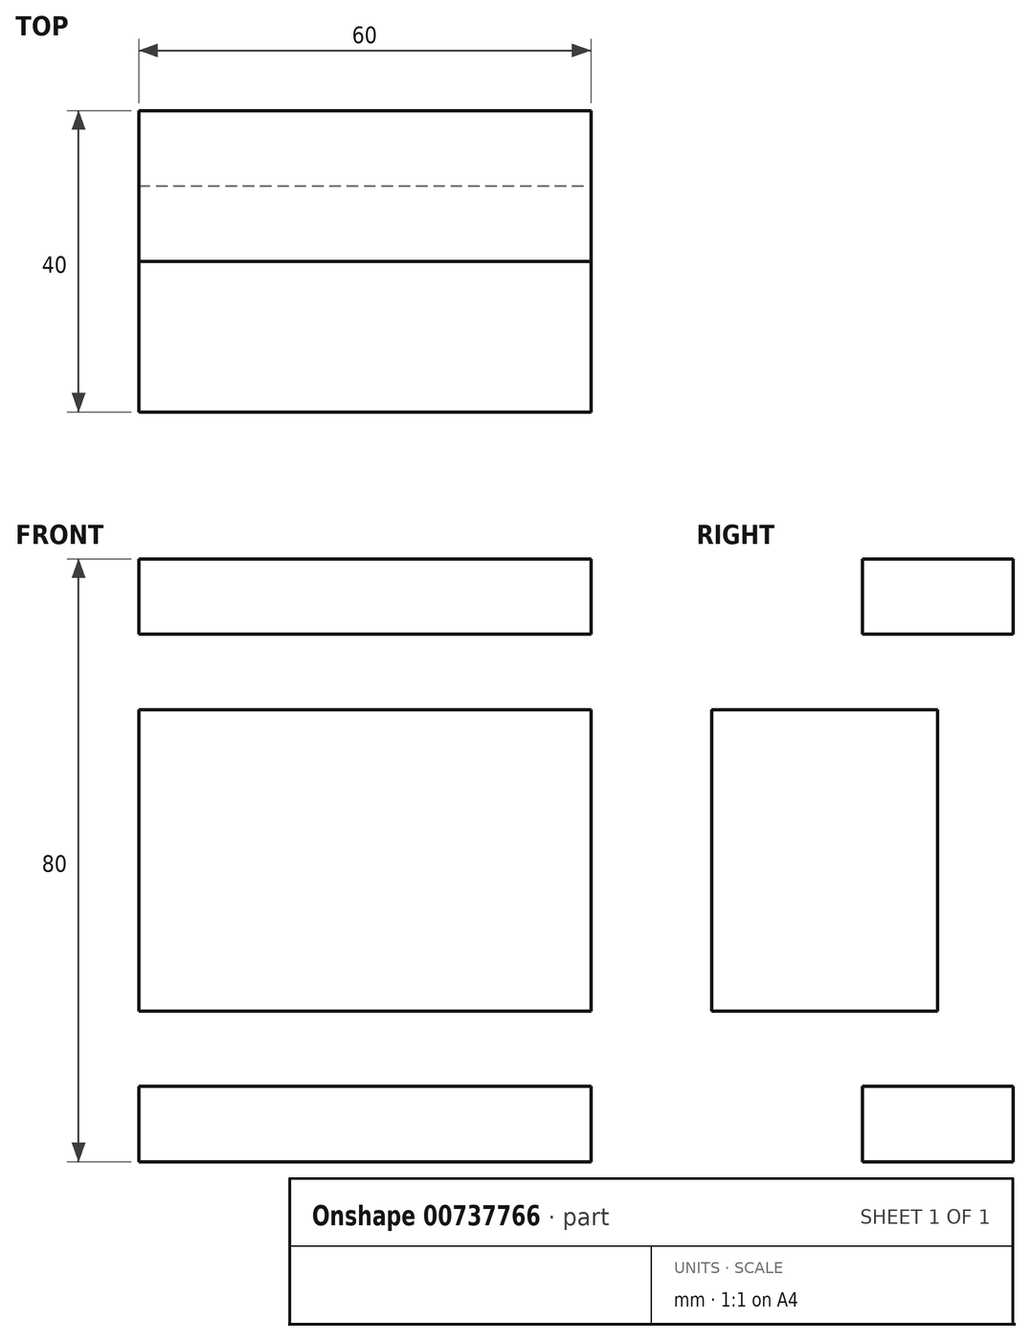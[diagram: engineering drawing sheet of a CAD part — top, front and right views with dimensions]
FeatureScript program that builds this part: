
annotation { "Feature Type Name" : "Feature", "Feature Type Description" : "" }
export const myFeature = defineFeature(function(context is Context, id is Id, definition is map)
    precondition{}
    {
        {
            var Q0;
            Q0=qCreatedBy(makeId("Front.planeOp"),FACE);
            var sketch = newSketch(context, id + "F0", { "sketchPlane" : qUnion([Q0])});
            skLineSegment(sketch, "E0.bottom", {"start": v(-36.66, -15.55) * mm, "end": v(23.34, -15.55) * mm});
            skLineSegment(sketch, "E0.top", {"start": v(-36.66, 24.45) * mm, "end": v(23.34, 24.45) * mm});
            skLineSegment(sketch, "E0.left", {"start": v(-36.66, -15.55) * mm, "end": v(-36.66, 24.45) * mm});
            skLineSegment(sketch, "E0.right", {"start": v(23.34, -15.55) * mm, "end": v(23.34, 24.45) * mm});
            skLineSegment(sketch, "E1.top", {"start": v(-36.66, 44.45) * mm, "end": v(23.34, 44.45) * mm});
            skLineSegment(sketch, "E1.left", {"start": v(-36.66, 24.45) * mm, "end": v(-36.66, 44.45) * mm});
            skLineSegment(sketch, "E1.right", {"start": v(23.34, 24.45) * mm, "end": v(23.34, 44.45) * mm});
            skLineSegment(sketch, "E2.bottom", {"start": v(23.34, -15.55) * mm, "end": v(-36.66, -15.55) * mm});
            skLineSegment(sketch, "E2.top", {"start": v(23.34, -35.55) * mm, "end": v(-36.66, -35.55) * mm});
            skLineSegment(sketch, "E2.left", {"start": v(23.34, -15.55) * mm, "end": v(23.34, -35.55) * mm});
            skLineSegment(sketch, "E2.right", {"start": v(-36.66, -15.55) * mm, "end": v(-36.66, -35.55) * mm});
            skLineSegment(sketch, "E3", {"start": v(-36.66, -25.55) * mm, "end": v(23.34, -25.55) * mm});
            skLineSegment(sketch, "E4", {"start": v(-36.66, 34.45) * mm, "end": v(23.34, 34.45) * mm});
            skSolve(sketch);
        }
        {
            var Q0;
            Q0=makeQuery(id+"F0.imprint","IMPRINT",FACE,{"disambiguationData":[TD([[makeQuery(id+"F0.imprint","IMPRINT",EDGE,{"derivedFrom":sQuery(id+"F0.wireOp",EDGE,"E0.left")}),-1.0]])]});
            extrude(context, id + "F1", {"entities" : qUnion([Q0]), "depth" : 30 * mm, "offsetDistance" : 25 * mm});
        }
        {
            var Q0;
            Q0=makeQuery(id+"F0.imprint","IMPRINT",FACE,{"disambiguationData":[TD([[makeQuery(id+"F0.imprint","IMPRINT",EDGE,{"derivedFrom":sQuery(id+"F0.wireOp",EDGE,"E0.top")}),1.0]])]});
            var Q1;
            Q1=makeQuery(id+"F0.imprint","IMPRINT",FACE,{"disambiguationData":[TD([[makeQuery(id+"F0.imprint","IMPRINT",EDGE,{"derivedFrom":sQuery(id+"F0.wireOp",EDGE,"E2.bottom")}),1.0]])]});
            var Q2;
            {var subQ0=sQuery(id+"F0.wireOp",EDGE,"E1.top");Q2=makeQuery(id+"F0.imprint","IMPRINT",FACE,{"disambiguationData":[TD([[makeQuery(id+"F0.imprint","IMPRINT",EDGE,{"derivedFrom":subQ0}),-1.0]])]});}
            var Q3;
            {var subQ0=sQuery(id+"F0.wireOp",EDGE,"E2.top");Q3=makeQuery(id+"F0.imprint","IMPRINT",FACE,{"disambiguationData":[TD([[makeQuery(id+"F0.imprint","IMPRINT",EDGE,{"derivedFrom":subQ0}),-1.0]])]});}
            extrude(context, id + "F2", {"entities" : qUnion([Q0, Q1, Q2, Q3]), "operationType" : NewBodyOperationType.ADD, "depth" : 10 * mm, "offsetDistance" : 25 * mm});
        }
        {
            var Q0;
            {var subQ0=sQuery(id+"F0.wireOp",EDGE,"E2.top");Q0=makeQuery(id+"F0.imprint","IMPRINT",FACE,{"disambiguationData":[TD([[makeQuery(id+"F0.imprint","IMPRINT",EDGE,{"derivedFrom":subQ0}),-1.0]])]});}
            var Q1;
            {var subQ0=sQuery(id+"F0.wireOp",EDGE,"E1.top");Q1=makeQuery(id+"F0.imprint","IMPRINT",FACE,{"disambiguationData":[TD([[makeQuery(id+"F0.imprint","IMPRINT",EDGE,{"derivedFrom":subQ0}),-1.0]])]});}
            extrude(context, id + "F3", {"entities" : qUnion([Q0, Q1]), "operationType" : NewBodyOperationType.ADD, "oppositeDirection" : true, "depth" : 10 * mm, "offsetDistance" : 25 * mm});
        }
    });
